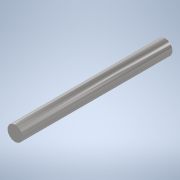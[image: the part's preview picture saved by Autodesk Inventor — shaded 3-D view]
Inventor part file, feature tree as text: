
AUTODESK INVENTOR PART (.ipt)
format: ipt  version: 2022 (Build 260153000, 153)  size: 95,744 bytes
history: native  units: in
note: dims shown in document units (in); Inventor stores cm internally (conversion verified against a paired STEP export)
features: extrude x1, sketch x1
ambient origin geometry x8: Origin, YZ Plane, XZ Plane, XY Plane, X Axis, Y Axis, Z Axis, Center Point
bodies: Solid1 (feature_tree)
feature tree (2):
  extrude  "Extrusion1"  Depth=3.9764in TaperAngle=0.0deg
  sketch  "Sketch1"  dims[d0=0.3937in d1=3.9764in d2=0.0in]
